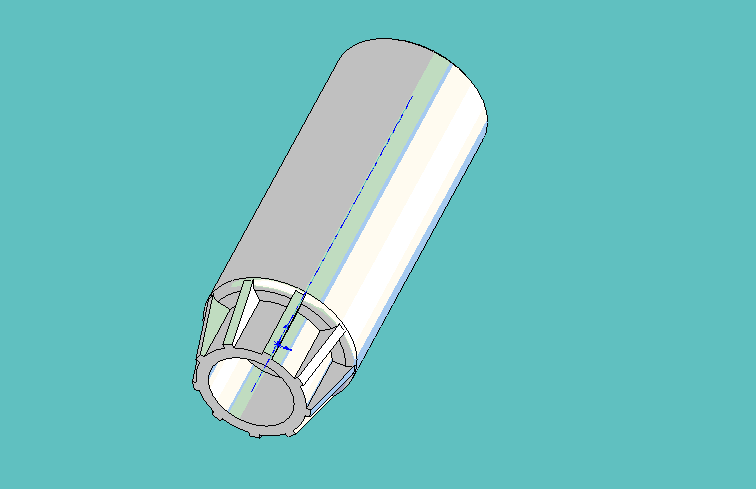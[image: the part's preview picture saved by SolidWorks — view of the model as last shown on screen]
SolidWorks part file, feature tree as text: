
SOLIDWORKS PART (.sldprt)
format: sldprt  version: not decoded by parser v0  size: 315,904 bytes
history: native  units: mm
features: sketch x7, extrude x4, plane x3, fillet x2, pattern_circular x2, material x1, cut_extrude x1, chamfer x1 (+10 scaffold rows collapsed)
feature tree (31):
  scaffold x10  (default folders/planes/origin — collapsed)
  material  "Material <not specified>"
  plane  "Frontal"
  plane  "Horizontal"
  plane  "Profile"
  sketch  "Sketch1"  dims[D1=~22.365295mm]
  extrude  "Extrude1"  Depth=84mm
  sketch  "Sketch2"
  extrude  "Extrude2"  Depth=2mm
  sketch  "Sketch3"  dims[D1=~7.885161mm]
  cut_extrude  "Cut-Extrude1"  [1 undecoded]
  sketch  "Sketch4"  dims[D1=~6.993245mm]
  extrude  "Extrude3"  Depth=1mm
  fillet  "Fillet1"  Radius=3mm
  fillet  "Fillet2"  Radius=2mm
  sketch  "Sketch5"  dims[D1=~11.445205mm]
  extrude  "Extrude4"  Depth=16mm
  sketch  "Sketch6"  dims[c1.D1=1.0mm c1.D2=3.0mm c2.D1=2.5mm]
  pattern_circular  "CirPattern1"  Count=9 Angle=360deg
  sketch  "Sketch7"  dims[c1.D1=2.0mm c1.D2=2.5mm c1.D3=~7.161642mm c2.D1=1.0mm]
  pattern_circular  "CirPattern2"  Count=4 Angle=360deg
  chamfer  "Chamfer1"  Distance=1mm Angle=45deg
decode coverage: 15 of 17 modeling features carry decoded parameters
note: ~ marks probable driven/reference dimensions
note: 1 parameter value undecoded
note: suppression state not decoded; provenance and decode notes live in map.json
